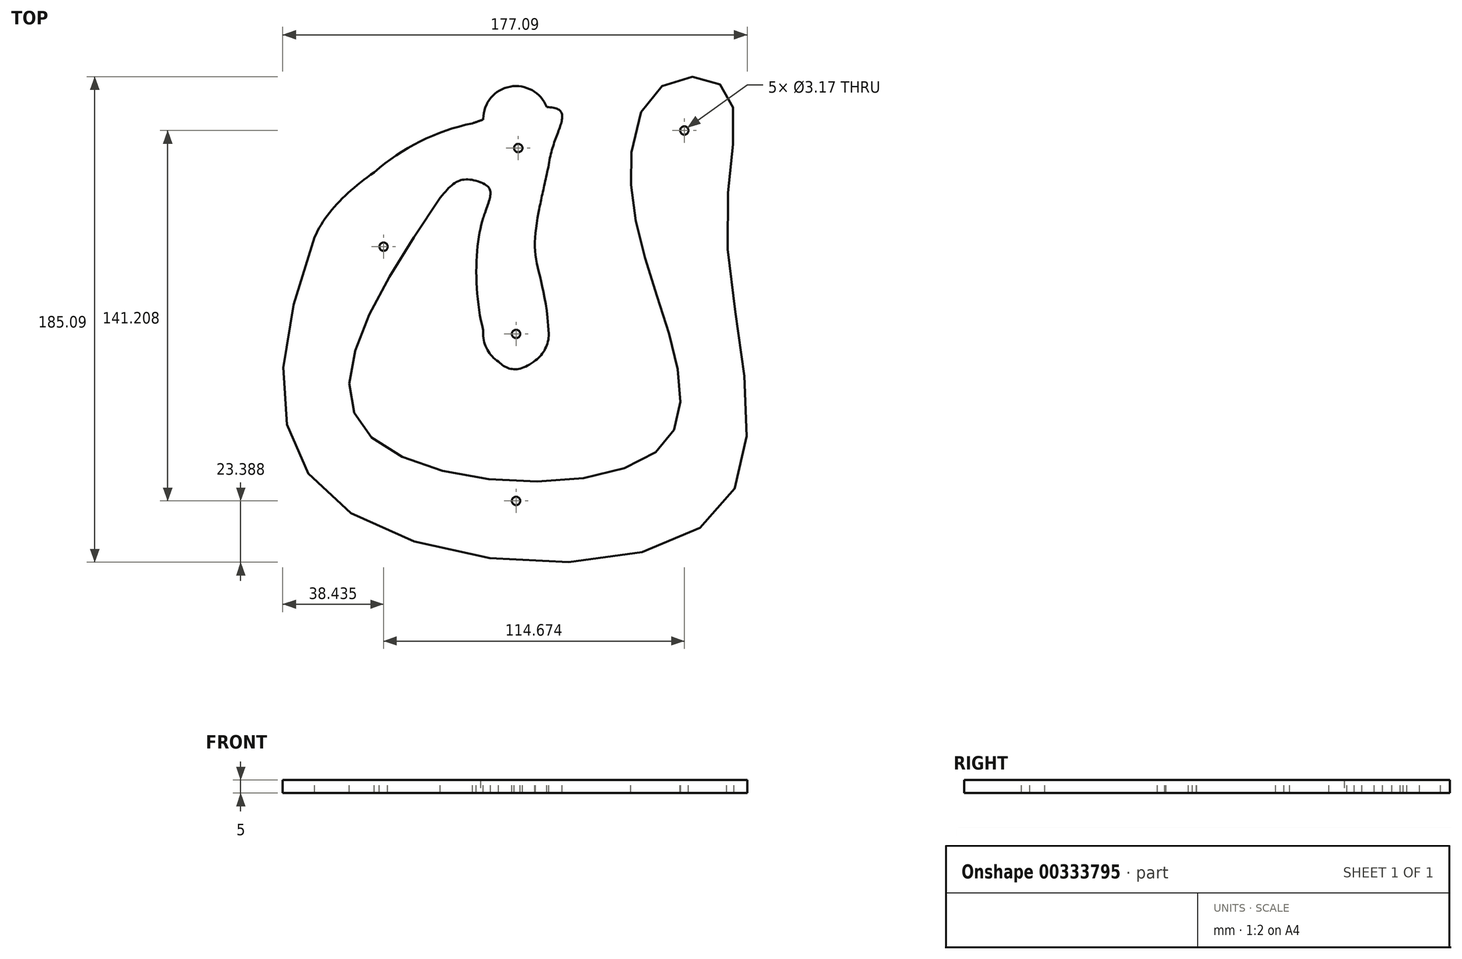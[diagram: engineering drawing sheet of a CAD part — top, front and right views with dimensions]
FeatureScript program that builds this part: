
annotation { "Feature Type Name" : "Feature", "Feature Type Description" : "" }
export const myFeature = defineFeature(function(context is Context, id is Id, definition is map)
    precondition{}
    {
        {
            var Q0;
            Q0=qCreatedBy(makeId("Top.planeOp"),FACE);
            var sketch = newSketch(context, id + "F0", { "sketchPlane" : qUnion([Q0])});
            skLineSegment(sketch, "E0.bottom", {"start": v(100, 100) * mm, "end": v(-100, 100) * mm});
            skLineSegment(sketch, "E0.top", {"start": v(100, -100) * mm, "end": v(-100, -100) * mm});
            skLineSegment(sketch, "E0.left", {"start": v(100, 100) * mm, "end": v(100, -100) * mm});
            skLineSegment(sketch, "E0.right", {"start": v(-100, 100) * mm, "end": v(-100, -100) * mm});
            skPoint(sketch, "E0.middle", {"position": v(0, 0) * mm});
            skSolve(sketch);
        }
        {
            var Q0;
            Q0=qSketchRegion(id+"F0",true);
            extrude(context, id + "F1", {"entities" : qUnion([Q0]), "depth" : 5 * mm});
        }
        {
            var Q0;
            Q0=makeQuery(id+"F1.opExtrude","CAP_FACE",FACE,{"disambiguationData":[OSD([sQuery(id+"F0.wireOp",EDGE,"E0.bottom"),sQuery(id+"F0.wireOp",EDGE,"E0.top"),sQuery(id+"F0.wireOp",EDGE,"E0.left"),sQuery(id+"F0.wireOp",EDGE,"E0.right")])],"isStart":false});
            var sketch = newSketch(context, id + "F2", { "sketchPlane" : qUnion([Q0])});
            skCircle(sketch, "E1", {"center": v(0, 0) * mm, "radius": 1.59 * mm});
            skCircle(sketch, "E2", {"center": v(0, -63.66) * mm, "radius": 1.59 * mm});
            skCircle(sketch, "E3", {"center": v(64.16, 77.55) * mm, "radius": 1.59 * mm});
            skCircle(sketch, "E4", {"center": v(-50.52, 33.26) * mm, "radius": 1.59 * mm});
            skCircle(sketch, "E5", {"center": v(0.85, 70.87) * mm, "radius": 1.59 * mm});
            skSolve(sketch);
        }
        {
            var Q0;
            Q0=qSketchRegion(id+"F2",true);
            extrude(context, id + "F3", {"entities" : qUnion([Q0]), "operationType" : NewBodyOperationType.REMOVE, "endBound" : BoundingType.THROUGH_ALL, "oppositeDirection" : true, "depth" : 25 * mm});
        }
        {
            var Q0;
            Q0=makeQuery(id+"F1.opExtrude","CAP_FACE",FACE,{"disambiguationData":[OSD([sQuery(id+"F0.wireOp",EDGE,"E0.bottom"),sQuery(id+"F0.wireOp",EDGE,"E0.top"),sQuery(id+"F0.wireOp",EDGE,"E0.left"),sQuery(id+"F0.wireOp",EDGE,"E0.right")])],"isStart":false});
            var sketch = newSketch(context, id + "F4", { "sketchPlane" : qUnion([Q0])});
            skCircle(sketch, "E6", {"center": v(0, 0) * mm, "radius": 82 * mm});
            skCircle(sketch, "E7", {"center": v(0, 0) * mm, "radius": 47 * mm});
            skLineSegment(sketch, "E8", {"start": v(0, 0) * mm, "end": v(0, 82) * mm});
            skArc(sketch, "E9.0.startCap", {"start": v(12.5, 0) * mm, "mid": v(0, -12.5) * mm, "end": v(-12.5, 0) * mm});
            skArc(sketch, "E9.0.endCap", {"start": v(-12.5, 82) * mm, "mid": v(0, 94.5) * mm, "end": v(12.5, 82) * mm});
            skLineSegment(sketch, "E9.0.left", {"start": v(-12.5, 0) * mm, "end": v(-12.5, 82) * mm});
            skLineSegment(sketch, "E9.0.right", {"start": v(12.5, 0) * mm, "end": v(12.5, 82) * mm});
            skFitSpline(sketch, "E10", {"points": [v(12.5, 0) * mm, v(7.29, 31.6) * mm, v(12.5, 64.57) * mm], "startDerivative": vector(-5.58, 100.77) * mm, "endDerivative": vector(19.92, 92.42) * mm});
            skFitSpline(sketch, "E11", {"points": [v(12.5, 64.57) * mm, v(15.9, 85.71) * mm, v(-76.77, 36.97) * mm], "startDerivative": vector(12.55, 103.21) * mm, "endDerivative": vector(-59.52, -138.77) * mm});
            skFitSpline(sketch, "E12", {"points": [v(-13.5, 57.84) * mm, v(-14.03, 37.96) * mm, v(7.39, -10.08) * mm], "startDerivative": vector(59.25, -24.3) * mm, "endDerivative": vector(96.36, 76.02) * mm});
            skFitSpline(sketch, "E13", {"points": [v(-76.77, 36.97) * mm, v(-68.06, -64.74) * mm, v(76.34, -68.92) * mm, v(80.41, 36.97) * mm, v(79.78, 93.34) * mm, v(54.94, 94.04) * mm, v(47, 36.97) * mm, v(55.5, -43.19) * mm, v(-56.73, -37.8) * mm, v(-28.87, 51.94) * mm], "startDerivative": vector(-365.44, -1013.64) * mm, "endDerivative": vector(584.88, 868.52) * mm});
            skFitSpline(sketch, "E14", {"points": [v(-28.87, 51.94) * mm, v(-13.5, 57.84) * mm], "startDerivative": vector(15.77, 19.88) * mm, "endDerivative": vector(21.6, -7.42) * mm});
            skSolve(sketch);
        }
        {
            var Q0;
            Q0=makeQuery(id+"F4.imprint","IMPRINT",FACE,{"disambiguationData":[TD([[makeQuery(id+"F4.imprint","IMPRINT",EDGE,{"derivedFrom":makeQuery(id+"F1.opExtrude","CAP_EDGE",EDGE,{"disambiguationData":[OSD([sQuery(id+"F0.wireOp",EDGE,"E0.bottom")])],"isStart":false})}),1.0]])]});
            var Q1;
            {var subQ5=sQuery(id+"F4.wireOp",EDGE,"E14");Q1=makeQuery(id+"F4.imprint","IMPRINT",FACE,{"disambiguationData":[TD([[makeQuery(id+"F4.imprint","IMPRINT",EDGE,{"derivedFrom":subQ5}),-1.0]])]});}
            var Q2;
            {var subQ7=sQuery(id+"F4.wireOp",EDGE,"E9.0.right");var subQ10=sQuery(id+"F4.wireOp",EDGE,"E7");var subQ11=makeQuery(id+"F4.imprint","INTERSECT",VERTEX,{"derivedFrom":[subQ10,subQ7]});Q2=makeQuery(id+"F4.imprint","IMPRINT",FACE,{"disambiguationData":[TD([[makeQuery(id+"F4.imprint","IMPRINT",EDGE,{"disambiguationData":[TD([[subQ11,1.0]])],"derivedFrom":subQ10}),1.0]])]});}
            var Q3;
            {var subQ0=sQuery(id+"F4.wireOp",EDGE,"E10");var subQ1=sQuery(id+"F4.wireOp",EDGE,"E7");var subQ2=makeQuery(id+"F4.imprint","INTERSECT",VERTEX,{"derivedFrom":[subQ1,subQ0]});Q3=makeQuery(id+"F4.imprint","IMPRINT",FACE,{"disambiguationData":[TD([[makeQuery(id+"F4.imprint","IMPRINT",EDGE,{"disambiguationData":[TD([[subQ2,1.0]])],"derivedFrom":subQ1}),1.0]])]});}
            var Q4;
            {var subQ0=sQuery(id+"F4.wireOp",EDGE,"E9.0.left");var subQ1=sQuery(id+"F4.wireOp",EDGE,"E9.0.startCap");var subQ2=makeQuery(id+"F4.imprint","INTERSECT",VERTEX,{"derivedFrom":[subQ1,subQ0]});Q4=makeQuery(id+"F4.imprint","IMPRINT",FACE,{"disambiguationData":[TD([[makeQuery(id+"F4.imprint","IMPRINT",EDGE,{"disambiguationData":[TD([[subQ2,1.0]])],"derivedFrom":subQ1}),-1.0]])]});}
            var Q5;
            {var subQ0=sQuery(id+"F4.wireOp",EDGE,"E9.0.left");var subQ1=sQuery(id+"F4.wireOp",EDGE,"E9.0.endCap");var subQ2=makeQuery(id+"F4.imprint","INTERSECT",VERTEX,{"derivedFrom":[subQ1,subQ0]});Q5=makeQuery(id+"F4.imprint","IMPRINT",FACE,{"disambiguationData":[TD([[makeQuery(id+"F4.imprint","IMPRINT",EDGE,{"disambiguationData":[TD([[subQ2,-1.0]])],"derivedFrom":subQ1}),-1.0]])]});}
            var Q6;
            {var subQ0=sQuery(id+"F4.wireOp",EDGE,"E10");var subQ1=sQuery(id+"F4.wireOp",EDGE,"E7");var subQ2=makeQuery(id+"F4.imprint","INTERSECT",VERTEX,{"derivedFrom":[subQ1,subQ0]});Q6=makeQuery(id+"F4.imprint","IMPRINT",FACE,{"disambiguationData":[TD([[makeQuery(id+"F4.imprint","IMPRINT",EDGE,{"disambiguationData":[TD([[subQ2,1.0]])],"derivedFrom":subQ1}),-1.0]])]});}
            var Q7;
            {var subQ0=sQuery(id+"F4.wireOp",EDGE,"E12");var subQ1=sQuery(id+"F4.wireOp",EDGE,"E7");var subQ2=makeQuery(id+"F4.imprint","INTERSECT",VERTEX,{"derivedFrom":[subQ1,subQ0]});Q7=makeQuery(id+"F4.imprint","IMPRINT",FACE,{"disambiguationData":[TD([[makeQuery(id+"F4.imprint","IMPRINT",EDGE,{"disambiguationData":[TD([[subQ2,-1.0]])],"derivedFrom":subQ1}),-1.0]])]});}
            var Q8;
            {var subQ0=sQuery(id+"F4.wireOp",EDGE,"E12");var subQ1=sQuery(id+"F4.wireOp",EDGE,"E7");var subQ2=makeQuery(id+"F4.imprint","INTERSECT",VERTEX,{"derivedFrom":[subQ1,subQ0]});Q8=makeQuery(id+"F4.imprint","IMPRINT",FACE,{"disambiguationData":[TD([[makeQuery(id+"F4.imprint","IMPRINT",EDGE,{"disambiguationData":[TD([[subQ2,-1.0]])],"derivedFrom":subQ1}),1.0]])]});}
            extrude(context, id + "F5", {"entities" : qUnion([Q0, Q1, Q2, Q3, Q4, Q5, Q6, Q7, Q8]), "operationType" : NewBodyOperationType.REMOVE, "endBound" : BoundingType.THROUGH_ALL, "oppositeDirection" : true, "depth" : 25 * mm});
        }
    });
